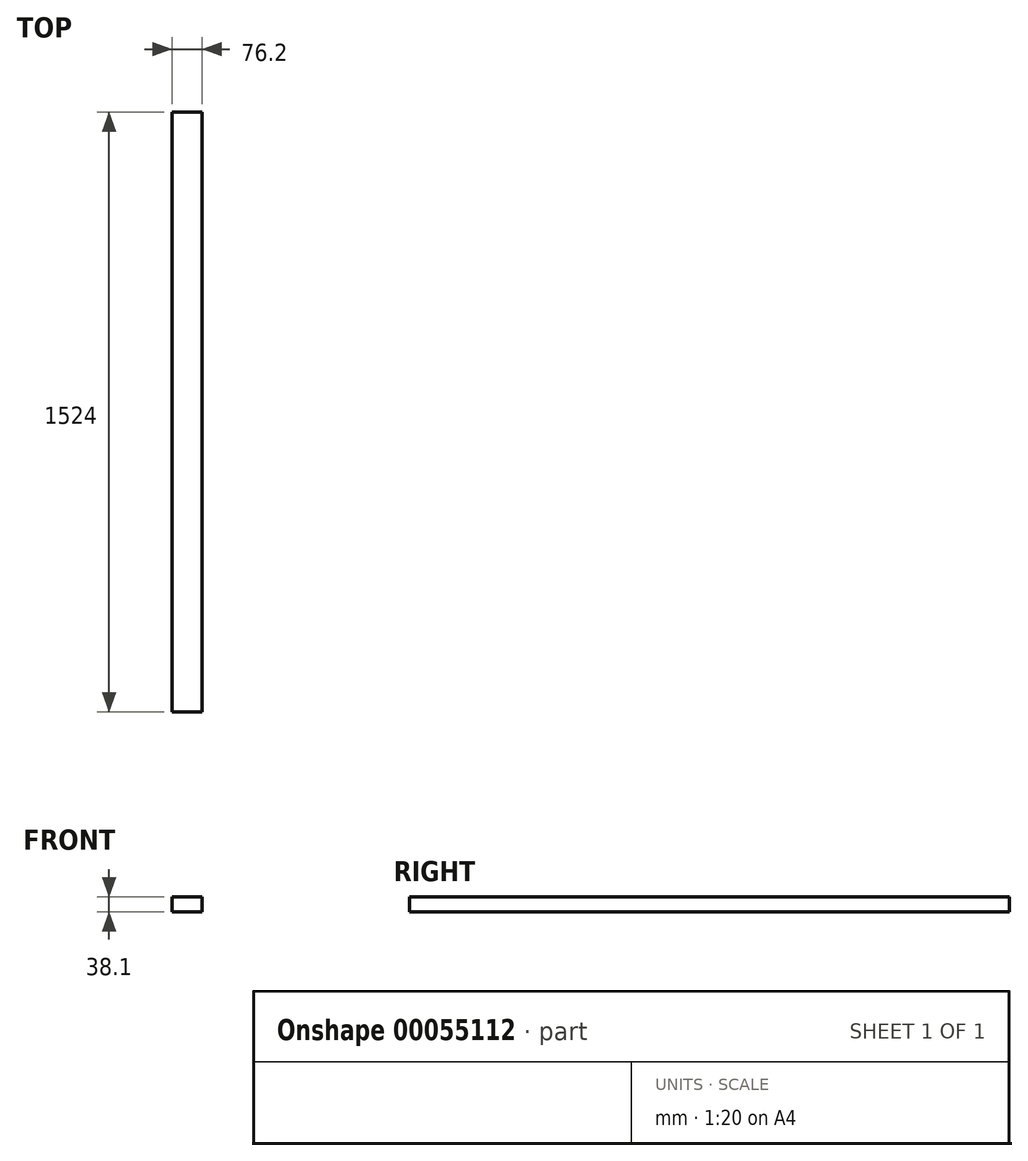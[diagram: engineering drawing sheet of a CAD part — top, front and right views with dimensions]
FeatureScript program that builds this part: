
annotation { "Feature Type Name" : "Feature", "Feature Type Description" : "" }
export const myFeature = defineFeature(function(context is Context, id is Id, definition is map)
    precondition{}
    {
        {
            var Q0;
            Q0=qCreatedBy(makeId("Front.planeOp"),FACE);
            var sketch = newSketch(context, id + "F0", { "sketchPlane" : qUnion([Q0])});
            skLineSegment(sketch, "E0.bottom", {"start": v(-37.66, -19.27) * mm, "end": v(38.54, -19.27) * mm});
            skLineSegment(sketch, "E0.top", {"start": v(-37.66, 18.83) * mm, "end": v(38.54, 18.83) * mm});
            skLineSegment(sketch, "E0.left", {"start": v(-37.66, -19.27) * mm, "end": v(-37.66, 18.83) * mm});
            skLineSegment(sketch, "E0.right", {"start": v(38.54, -19.27) * mm, "end": v(38.54, 18.83) * mm});
            skLineSegment(sketch, "E1", {"start": v(-37.66, 18.83) * mm, "end": v(0.44, -0.22) * mm, "construction": true});
            skLineSegment(sketch, "E2", {"start": v(0.44, -0.22) * mm, "end": v(38.54, -19.27) * mm, "construction": true});
            skSolve(sketch);
        }
        {
            var Q0;
            Q0 = qSketchRegion(id + "F0", true);
            extrude(context, id + "F1", {"entities" : qUnion([Q0]), "depth" : 1524 * mm});
        }
    });
